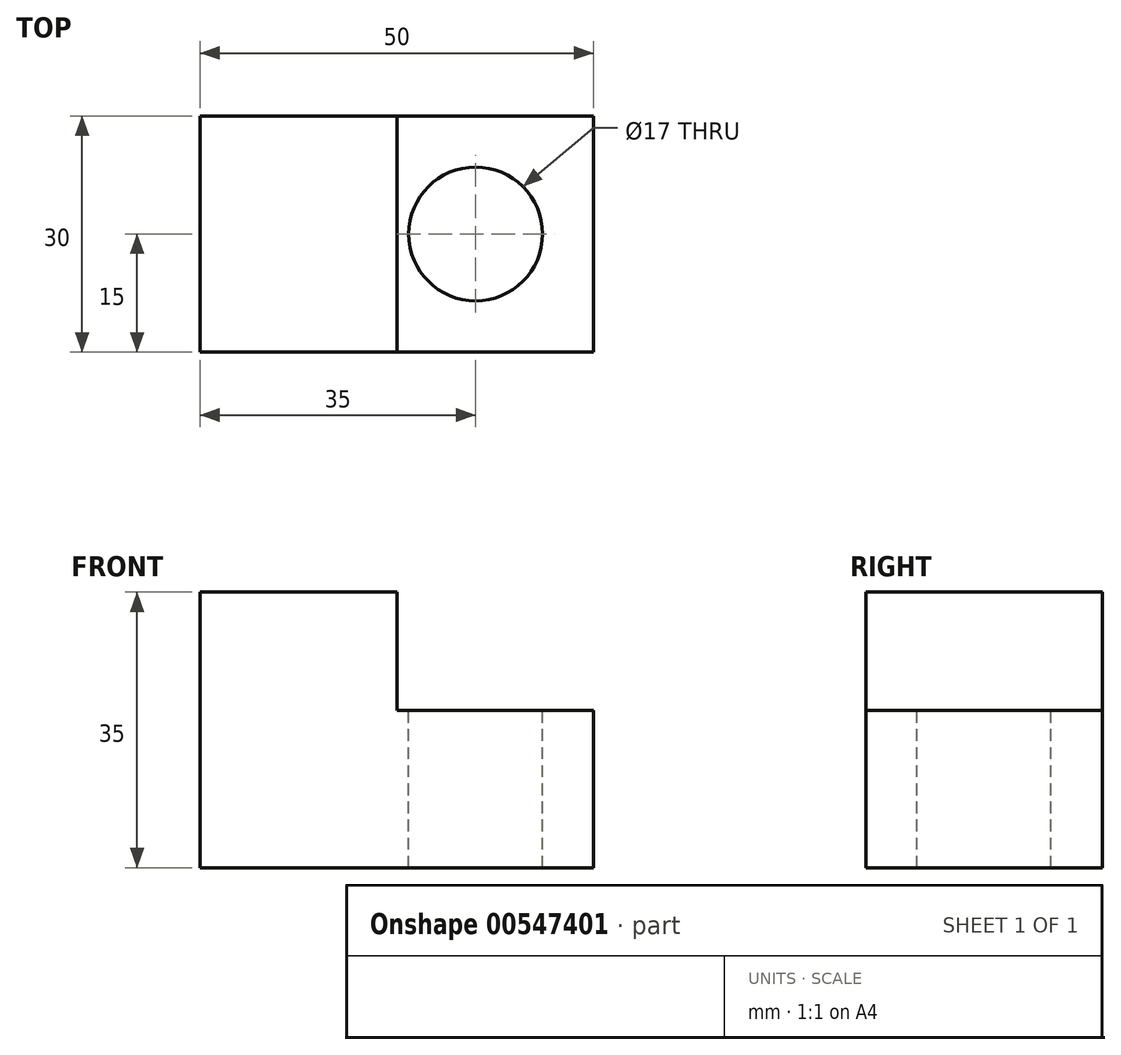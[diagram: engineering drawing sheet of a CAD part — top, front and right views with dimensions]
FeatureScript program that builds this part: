
annotation { "Feature Type Name" : "Feature", "Feature Type Description" : "" }
export const myFeature = defineFeature(function(context is Context, id is Id, definition is map)
    precondition{}
    {
        {
            var Q0;
            Q0=qCreatedBy(makeId("Front.planeOp"),FACE);
            var sketch = newSketch(context, id + "F0", { "sketchPlane" : qUnion([Q0])});
            skLineSegment(sketch, "E0.bottom", {"start": v(0, 0) * mm, "end": v(50, 0) * mm});
            skLineSegment(sketch, "E0.top", {"start": v(0, 35) * mm, "end": v(50, 35) * mm});
            skLineSegment(sketch, "E0.left", {"start": v(0, 0) * mm, "end": v(0, 35) * mm});
            skLineSegment(sketch, "E0.right", {"start": v(50, 0) * mm, "end": v(50, 35) * mm});
            skSolve(sketch);
        }
        {
            var Q0;
            Q0=qSketchRegion(id+"F0",true);
            extrude(context, id + "F1", {"entities" : qUnion([Q0]), "depth" : 30 * mm, "offsetDistance" : 25.4 * mm});
        }
        {
            var Q0;
            Q0=makeQuery(id+"F1.opExtrude","CAP_FACE",FACE,{"disambiguationData":[OSD([sQuery(id+"F0.wireOp",EDGE,"E0.bottom"),sQuery(id+"F0.wireOp",EDGE,"E0.top"),sQuery(id+"F0.wireOp",EDGE,"E0.left"),sQuery(id+"F0.wireOp",EDGE,"E0.right")])],"isStart":false});
            var sketch = newSketch(context, id + "F2", { "sketchPlane" : qUnion([Q0])});
            skLineSegment(sketch, "E1.bottom", {"start": v(50, 35) * mm, "end": v(25, 35) * mm});
            skLineSegment(sketch, "E1.top", {"start": v(50, 20) * mm, "end": v(25, 20) * mm});
            skLineSegment(sketch, "E1.left", {"start": v(50, 35) * mm, "end": v(50, 20) * mm});
            skLineSegment(sketch, "E1.right", {"start": v(25, 35) * mm, "end": v(25, 20) * mm});
            skSolve(sketch);
        }
        {
            var Q0;
            Q0=qSketchRegion(id+"F2",true);
            extrude(context, id + "F3", {"entities" : qUnion([Q0]), "operationType" : NewBodyOperationType.REMOVE, "endBound" : BoundingType.THROUGH_ALL, "oppositeDirection" : true, "depth" : 25.4 * mm, "offsetDistance" : 25.4 * mm});
        }
        {
            var Q0;
            Q0=makeQuery(id+"F3.boolean.opBoolean","COPY",FACE,{"derivedFrom":makeQuery(id+"F3.opExtrude","SWEPT_FACE",FACE,{"disambiguationData":[OSD([sQuery(id+"F2.wireOp",EDGE,"E1.top")])]})});
            var sketch = newSketch(context, id + "F4", { "sketchPlane" : qUnion([Q0])});
            skCircle(sketch, "E2", {"center": v(35, -15) * mm, "radius": 8.5 * mm});
            skSolve(sketch);
        }
        {
            var Q0;
            Q0=qSketchRegion(id+"F4",true);
            extrude(context, id + "F5", {"entities" : qUnion([Q0]), "operationType" : NewBodyOperationType.REMOVE, "endBound" : BoundingType.THROUGH_ALL, "oppositeDirection" : true, "depth" : 25.4 * mm, "offsetDistance" : 25.4 * mm});
        }
    });
